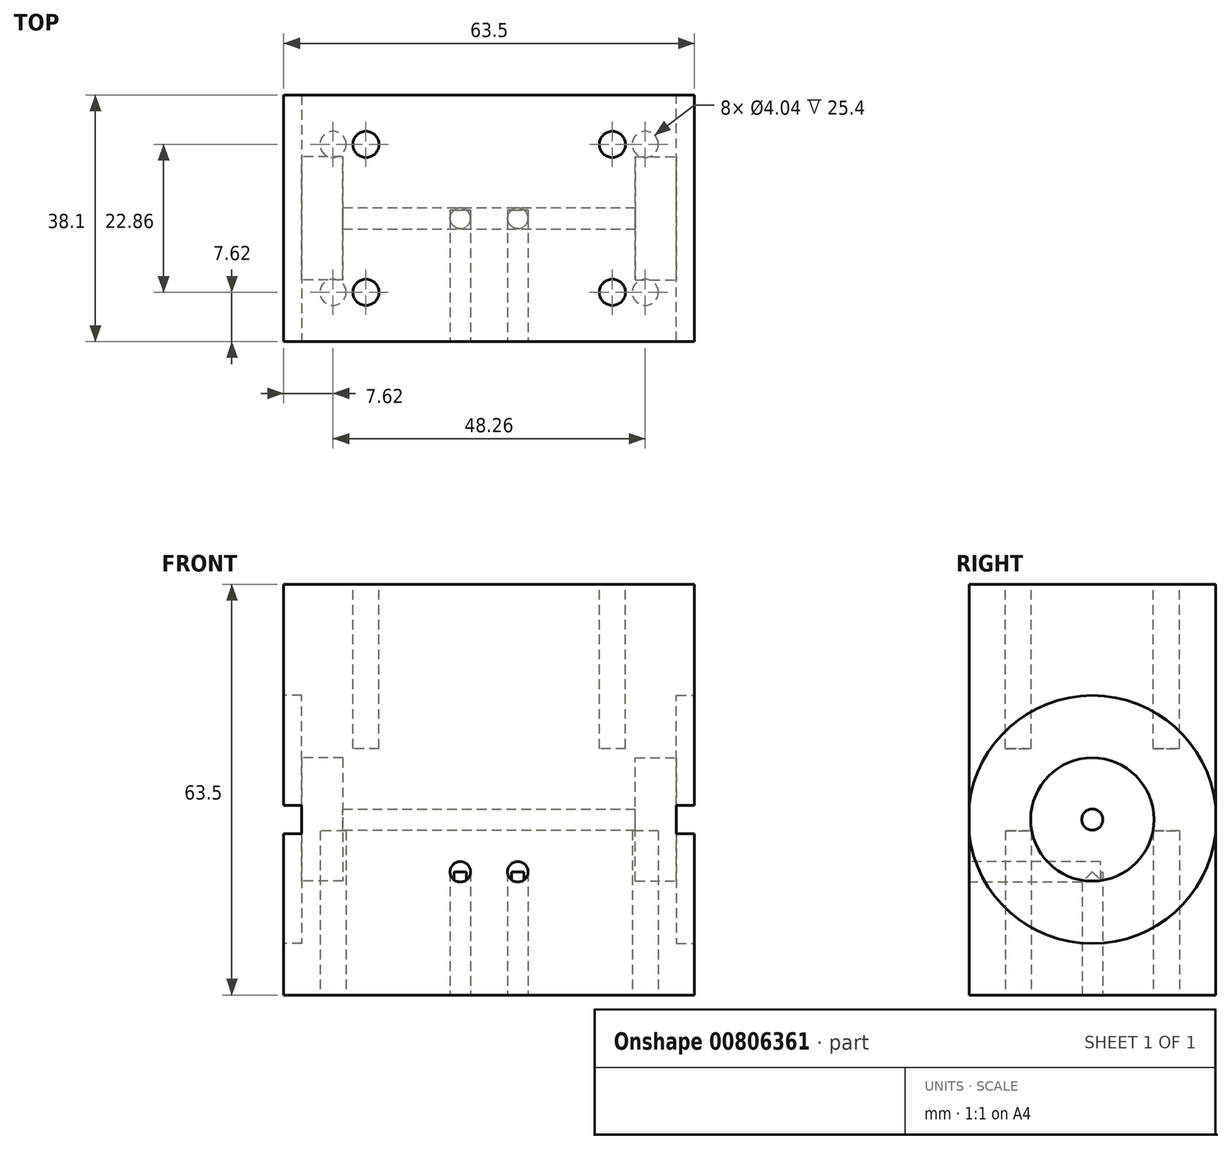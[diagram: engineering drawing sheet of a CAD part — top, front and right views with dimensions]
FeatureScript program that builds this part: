
annotation { "Feature Type Name" : "Feature", "Feature Type Description" : "" }
export const myFeature = defineFeature(function(context is Context, id is Id, definition is map)
    precondition{}
    {
        {
            var Q0;
            Q0=qCreatedBy(makeId("Top.planeOp"),FACE);
            var sketch = newSketch(context, id + "F0", { "sketchPlane" : qUnion([Q0])});
            skLineSegment(sketch, "E0.bottom", {"start": v(31.75, 19.05) * mm, "end": v(-31.75, 19.05) * mm});
            skLineSegment(sketch, "E0.top", {"start": v(31.75, -19.05) * mm, "end": v(-31.75, -19.05) * mm});
            skLineSegment(sketch, "E0.left", {"start": v(31.75, 19.05) * mm, "end": v(31.75, -19.05) * mm});
            skLineSegment(sketch, "E0.right", {"start": v(-31.75, 19.05) * mm, "end": v(-31.75, -19.05) * mm});
            skPoint(sketch, "E0.middle", {"position": v(0, 0) * mm});
            skCircle(sketch, "E1", {"center": v(-24.13, 11.43) * mm, "radius": 2.02 * mm});
            skCircle(sketch, "E2", {"center": v(24.13, 11.43) * mm, "radius": 2.02 * mm});
            skCircle(sketch, "E3", {"center": v(24.13, -11.43) * mm, "radius": 2.02 * mm});
            skCircle(sketch, "E4", {"center": v(-24.13, -11.43) * mm, "radius": 2.02 * mm});
            skSolve(sketch);
        }
        {
            var Q0;
            Q0=makeQuery(id+"F0.imprint","IMPRINT",FACE,{"disambiguationData":[TD([[makeQuery(id+"F0.imprint","IMPRINT",EDGE,{"derivedFrom":sQuery(id+"F0.wireOp",EDGE,"E1")}),1.0]])]});
            var Q1;
            Q1=makeQuery(id+"F0.imprint","IMPRINT",FACE,{"disambiguationData":[TD([[makeQuery(id+"F0.imprint","IMPRINT",EDGE,{"derivedFrom":sQuery(id+"F0.wireOp",EDGE,"E2")}),1.0]])]});
            var Q2;
            Q2=makeQuery(id+"F0.imprint","IMPRINT",FACE,{"disambiguationData":[TD([[makeQuery(id+"F0.imprint","IMPRINT",EDGE,{"derivedFrom":sQuery(id+"F0.wireOp",EDGE,"E3")}),1.0]])]});
            var Q3;
            Q3=makeQuery(id+"F0.imprint","IMPRINT",FACE,{"disambiguationData":[TD([[makeQuery(id+"F0.imprint","IMPRINT",EDGE,{"derivedFrom":sQuery(id+"F0.wireOp",EDGE,"E4")}),1.0]])]});
            var Q4;
            Q4=makeQuery(id+"F0.imprint","IMPRINT",FACE,{"disambiguationData":[TD([[makeQuery(id+"F0.imprint","IMPRINT",EDGE,{"derivedFrom":sQuery(id+"F0.wireOp",EDGE,"E0.bottom")}),1.0]])]});
            extrude(context, id + "F1", {"entities" : qUnion([Q0, Q1, Q2, Q3, Q4]), "depth" : 63.5 * mm, "offsetDistance" : 25.4 * mm});
        }
        {
            var Q0;
            Q0=makeQuery(id+"F0.imprint","IMPRINT",FACE,{"disambiguationData":[TD([[makeQuery(id+"F0.imprint","IMPRINT",EDGE,{"derivedFrom":sQuery(id+"F0.wireOp",EDGE,"E2")}),1.0]])]});
            var Q1;
            Q1=makeQuery(id+"F0.imprint","IMPRINT",FACE,{"disambiguationData":[TD([[makeQuery(id+"F0.imprint","IMPRINT",EDGE,{"derivedFrom":sQuery(id+"F0.wireOp",EDGE,"E3")}),1.0]])]});
            var Q2;
            Q2=makeQuery(id+"F0.imprint","IMPRINT",FACE,{"disambiguationData":[TD([[makeQuery(id+"F0.imprint","IMPRINT",EDGE,{"derivedFrom":sQuery(id+"F0.wireOp",EDGE,"E1")}),1.0]])]});
            var Q3;
            Q3=makeQuery(id+"F0.imprint","IMPRINT",FACE,{"disambiguationData":[TD([[makeQuery(id+"F0.imprint","IMPRINT",EDGE,{"derivedFrom":sQuery(id+"F0.wireOp",EDGE,"E4")}),1.0]])]});
            extrude(context, id + "F2", {"entities" : qUnion([Q0, Q1, Q2, Q3]), "operationType" : NewBodyOperationType.REMOVE, "depth" : 25.4 * mm, "offsetDistance" : 25.4 * mm});
        }
        {
            var Q0;
            Q0=makeQuery(id+"F1.opExtrude","CAP_FACE",FACE,{"disambiguationData":[OSD([sQuery(id+"F0.wireOp",EDGE,"E0.bottom"),sQuery(id+"F0.wireOp",EDGE,"E0.top"),sQuery(id+"F0.wireOp",EDGE,"E0.left"),sQuery(id+"F0.wireOp",EDGE,"E0.right")])],"isStart":false});
            var sketch = newSketch(context, id + "F3", { "sketchPlane" : qUnion([Q0])});
            skCircle(sketch, "E5", {"center": v(-19.05, 11.43) * mm, "radius": 2.02 * mm});
            skCircle(sketch, "E6", {"center": v(-19.05, -11.43) * mm, "radius": 2.02 * mm});
            skCircle(sketch, "E7", {"center": v(19.05, 11.43) * mm, "radius": 2.02 * mm});
            skCircle(sketch, "E8", {"center": v(19.05, -11.43) * mm, "radius": 2.02 * mm});
            skSolve(sketch);
        }
        {
            var Q0;
            Q0 = qSketchRegion(id + "F3", true);
            extrude(context, id + "F4", {"entities" : qUnion([Q0]), "operationType" : NewBodyOperationType.REMOVE, "oppositeDirection" : true, "depth" : 25.4 * mm, "offsetDistance" : 25.4 * mm});
        }
        {
            var Q0;
            Q0=makeQuery(id+"F0.imprint","IMPRINT",FACE,{"disambiguationData":[TD([[makeQuery(id+"F0.imprint","IMPRINT",EDGE,{"derivedFrom":sQuery(id+"F0.wireOp",EDGE,"E0.bottom")}),1.0]])]});
            var sketch = newSketch(context, id + "F5", { "sketchPlane" : qUnion([Q0])});
            skCircle(sketch, "E9", {"center": v(-4.45, 0) * mm, "radius": 1.59 * mm});
            skCircle(sketch, "E10", {"center": v(4.45, 0) * mm, "radius": 1.59 * mm});
            skCircle(sketch, "E11", {"center": v(0, 0) * mm, "radius": 8.9 * mm});
            skSolve(sketch);
        }
        {
            var Q0;
            Q0=makeQuery(id+"F5.imprint","IMPRINT",FACE,{"disambiguationData":[TD([[makeQuery(id+"F5.imprint","IMPRINT",EDGE,{"derivedFrom":sQuery(id+"F5.wireOp",EDGE,"E9")}),1.0]])]});
            var Q1;
            Q1=makeQuery(id+"F5.imprint","IMPRINT",FACE,{"disambiguationData":[TD([[makeQuery(id+"F5.imprint","IMPRINT",EDGE,{"derivedFrom":sQuery(id+"F5.wireOp",EDGE,"E10")}),1.0]])]});
            extrude(context, id + "F6", {"entities" : qUnion([Q0, Q1]), "operationType" : NewBodyOperationType.REMOVE, "depth" : 19.05 * mm, "offsetDistance" : 25.4 * mm});
        }
        {
            var Q0;
            Q0=makeQuery(id+"F1.opExtrude","SWEPT_FACE",FACE,{"disambiguationData":[OSD([sQuery(id+"F0.wireOp",EDGE,"E0.top")])]});
            var sketch = newSketch(context, id + "F7", { "sketchPlane" : qUnion([Q0])});
            skCircle(sketch, "E12", {"center": v(-4.45, 19.05) * mm, "radius": 1.59 * mm});
            skCircle(sketch, "E13", {"center": v(4.45, 19.05) * mm, "radius": 1.59 * mm});
            skSolve(sketch);
        }
        {
            var Q0;
            Q0 = qSketchRegion(id + "F7", true);
            extrude(context, id + "F8", {"entities" : qUnion([Q0]), "operationType" : NewBodyOperationType.REMOVE, "oppositeDirection" : true, "depth" : 20.32 * mm, "offsetDistance" : 25.4 * mm});
        }
        {
            var Q0;
            Q0=makeQuery(id+"F1.opExtrude","SWEPT_FACE",FACE,{"disambiguationData":[OSD([sQuery(id+"F0.wireOp",EDGE,"E0.left")])]});
            var sketch = newSketch(context, id + "F9", { "sketchPlane" : qUnion([Q0])});
            skCircle(sketch, "E14", {"center": v(0, 27.13) * mm, "radius": 1.63 * mm});
            skCircle(sketch, "E15", {"center": v(0, 27.13) * mm, "radius": 9.53 * mm});
            skCircle(sketch, "E16", {"center": v(0, 27.13) * mm, "radius": 19.18 * mm});
            skSolve(sketch);
        }
        {
            var Q0;
            Q0=makeQuery(id+"F9.imprint","IMPRINT",FACE,{"disambiguationData":[TD([[makeQuery(id+"F9.imprint","IMPRINT",EDGE,{"derivedFrom":sQuery(id+"F9.wireOp",EDGE,"E14")}),1.0]])]});
            extrude(context, id + "F10", {"entities" : qUnion([Q0]), "operationType" : NewBodyOperationType.REMOVE, "endBound" : BoundingType.THROUGH_ALL, "oppositeDirection" : true, "depth" : 25.4 * mm, "offsetDistance" : 25.4 * mm});
        }
        {
            var Q0;
            Q0=makeQuery(id+"F9.imprint","IMPRINT",FACE,{"disambiguationData":[TD([[makeQuery(id+"F9.imprint","IMPRINT",EDGE,{"derivedFrom":sQuery(id+"F9.wireOp",EDGE,"E14")}),-1.0]])]});
            extrude(context, id + "F11", {"entities" : qUnion([Q0]), "operationType" : NewBodyOperationType.REMOVE, "oppositeDirection" : true, "depth" : 9.14 * mm, "offsetDistance" : 25.4 * mm});
        }
        {
            var Q0;
            Q0=makeQuery(id+"F9.imprint","IMPRINT",FACE,{"disambiguationData":[TD([[makeQuery(id+"F9.imprint","IMPRINT",EDGE,{"derivedFrom":sQuery(id+"F9.wireOp",EDGE,"E15")}),-1.0]])]});
            extrude(context, id + "F12", {"entities" : qUnion([Q0]), "operationType" : NewBodyOperationType.REMOVE, "oppositeDirection" : true, "depth" : 2.8 * mm, "offsetDistance" : 25.4 * mm});
        }
        {
            var Q0;
            Q0=makeQuery(id+"F1.opExtrude","SWEPT_FACE",FACE,{"disambiguationData":[OSD([sQuery(id+"F0.wireOp",EDGE,"E0.right")])]});
            var sketch = newSketch(context, id + "F13", { "sketchPlane" : qUnion([Q0])});
            skCircle(sketch, "E17", {"center": v(0, 27.13) * mm, "radius": 9.53 * mm});
            skCircle(sketch, "E18", {"center": v(0, 27.13) * mm, "radius": 19.18 * mm});
            skSolve(sketch);
        }
        {
            var Q0;
            Q0=makeQuery(id+"F13.imprint","IMPRINT",FACE,{"disambiguationData":[TD([[makeQuery(id+"F13.imprint","IMPRINT",EDGE,{"derivedFrom":sQuery(id+"F13.wireOp",EDGE,"E17")}),1.0]])]});
            extrude(context, id + "F14", {"entities" : qUnion([Q0]), "operationType" : NewBodyOperationType.REMOVE, "oppositeDirection" : true, "depth" : 9.14 * mm, "offsetDistance" : 25.4 * mm});
        }
        {
            var Q0;
            Q0=makeQuery(id+"F13.imprint","IMPRINT",FACE,{"disambiguationData":[TD([[makeQuery(id+"F13.imprint","IMPRINT",EDGE,{"derivedFrom":sQuery(id+"F13.wireOp",EDGE,"E17")}),-1.0]])]});
            extrude(context, id + "F15", {"entities" : qUnion([Q0]), "operationType" : NewBodyOperationType.REMOVE, "oppositeDirection" : true, "depth" : 2.8 * mm, "offsetDistance" : 25.4 * mm});
        }
    });
